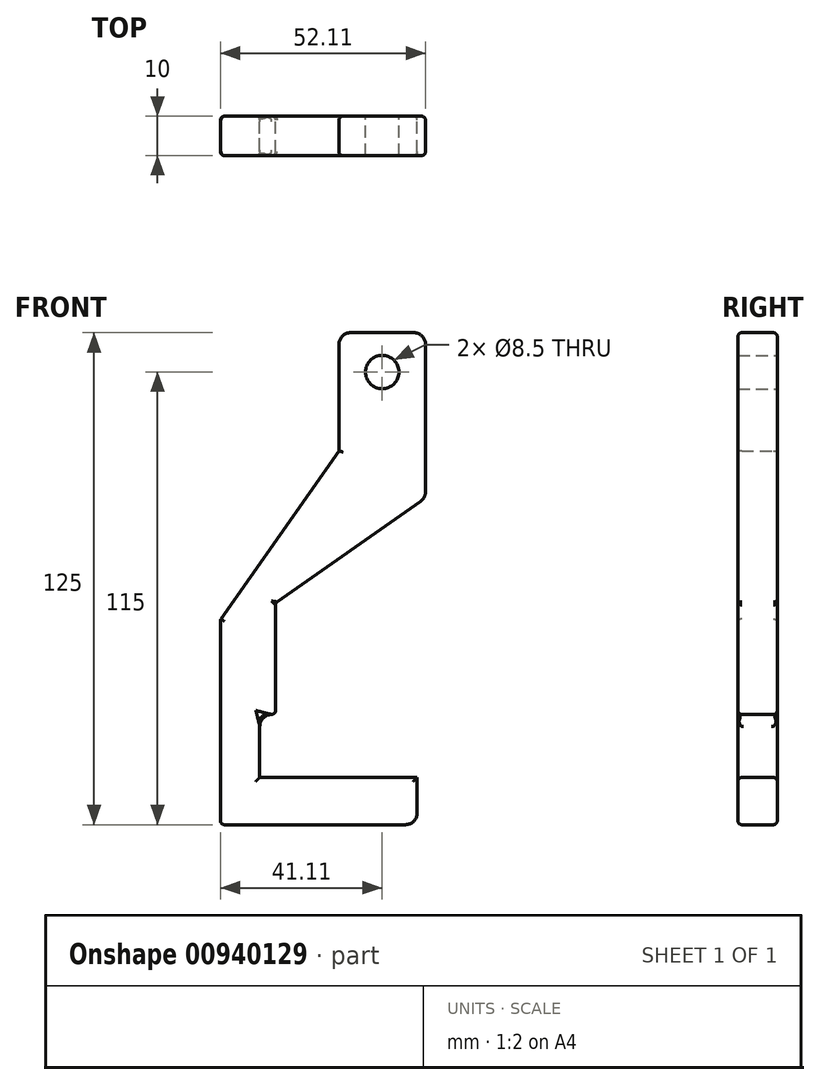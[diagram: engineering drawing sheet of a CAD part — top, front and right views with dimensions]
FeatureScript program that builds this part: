
annotation { "Feature Type Name" : "Feature", "Feature Type Description" : "" }
export const myFeature = defineFeature(function(context is Context, id is Id, definition is map)
    precondition{}
    {
        {
            var Q0;
            Q0=qCreatedBy(makeId("Front.planeOp"),FACE);
            var sketch = newSketch(context, id + "F0", { "sketchPlane" : qUnion([Q0])});
            skCircle(sketch, "E0", {"center": v(0, 0) * mm, "radius": 4.25 * mm});
            skLineSegment(sketch, "E1", {"start": v(0, 0) * mm, "end": v(0, 4.25) * mm});
            skLineSegment(sketch, "E2", {"start": v(0, 10) * mm, "end": v(-11, 10) * mm});
            skLineSegment(sketch, "E3", {"start": v(0, 10) * mm, "end": v(11, 10) * mm});
            skLineSegment(sketch, "E4", {"start": v(11, 10) * mm, "end": v(11, -32) * mm});
            skLineSegment(sketch, "E5", {"start": v(-11, 10) * mm, "end": v(-11, -20) * mm});
            skLineSegment(sketch, "E6", {"start": v(-41.1, -115) * mm, "end": v(-41.1, -63) * mm});
            skLineSegment(sketch, "E7", {"start": v(-41.1, -115) * mm, "end": v(8.9, -115) * mm});
            skLineSegment(sketch, "E8", {"start": v(8.9, -115) * mm, "end": v(8.9, -103) * mm});
            skLineSegment(sketch, "E9", {"start": v(8.9, -103) * mm, "end": v(-31.1, -103) * mm});
            skLineSegment(sketch, "E10", {"start": v(-31.1, -103) * mm, "end": v(-31.1, -87) * mm});
            skLineSegment(sketch, "E11", {"start": v(-31.1, -87) * mm, "end": v(-27.1, -87) * mm});
            skLineSegment(sketch, "E12", {"start": v(-27.1, -87) * mm, "end": v(-27.1, -58.68) * mm});
            skLineSegment(sketch, "E13", {"start": v(-41.1, -63) * mm, "end": v(-11, -20) * mm});
            skLineSegment(sketch, "E14", {"start": v(11, -32) * mm, "end": v(-27.1, -58.68) * mm});
            skSolve(sketch);
        }
        {
            var Q0;
            Q0=makeQuery(id+"F0.imprint","IMPRINT",FACE,{"disambiguationData":[TD([[makeQuery(id+"F0.imprint","IMPRINT",EDGE,{"derivedFrom":sQuery(id+"F0.wireOp",EDGE,"E0")}),-1.0]])]});
            extrude(context, id + "F1", {"entities" : qUnion([Q0]), "depth" : 10 * mm, "offsetDistance" : 25 * mm});
        }
        {
            var Q0;
            Q0=makeQuery(id+"F1.opExtrude","CAP_EDGE",EDGE,{"disambiguationData":[OSD([sQuery(id+"F0.wireOp",EDGE,"E5")])],"isStart":false});
            var Q1;
            Q1=makeQuery(id+"F1.opExtrude","CAP_EDGE",EDGE,{"disambiguationData":[OSD([sQuery(id+"F0.wireOp",EDGE,"E13")])],"isStart":false});
            var Q2;
            Q2=makeQuery(id+"F1.opExtrude","CAP_EDGE",EDGE,{"disambiguationData":[OSD([sQuery(id+"F0.wireOp",EDGE,"E6")])],"isStart":true});
            var Q3;
            Q3=makeQuery(id+"F1.opExtrude","CAP_EDGE",EDGE,{"disambiguationData":[OSD([sQuery(id+"F0.wireOp",EDGE,"E2"),sQuery(id+"F0.wireOp",EDGE,"E3")])],"isStart":false});
            var Q4;
            Q4=makeQuery(id+"F1.opExtrude","CAP_EDGE",EDGE,{"disambiguationData":[OSD([sQuery(id+"F0.wireOp",EDGE,"E4")])],"isStart":false});
            var Q5;
            Q5=makeQuery(id+"F1.opExtrude","CAP_EDGE",EDGE,{"disambiguationData":[OSD([sQuery(id+"F0.wireOp",EDGE,"E14")])],"isStart":false});
            var Q6;
            Q6=makeQuery(id+"F1.opExtrude","CAP_EDGE",EDGE,{"disambiguationData":[OSD([sQuery(id+"F0.wireOp",EDGE,"E12")])],"isStart":false});
            var Q7;
            Q7=makeQuery(id+"F1.opExtrude","CAP_EDGE",EDGE,{"disambiguationData":[OSD([sQuery(id+"F0.wireOp",EDGE,"E7")])],"isStart":false});
            var Q8;
            Q8=makeQuery(id+"F1.opExtrude","CAP_EDGE",EDGE,{"disambiguationData":[OSD([sQuery(id+"F0.wireOp",EDGE,"E8")])],"isStart":false});
            var Q9;
            Q9=makeQuery(id+"F1.opExtrude","CAP_EDGE",EDGE,{"disambiguationData":[OSD([sQuery(id+"F0.wireOp",EDGE,"E9")])],"isStart":false});
            var Q10;
            Q10=makeQuery(id+"F1.opExtrude","CAP_EDGE",EDGE,{"disambiguationData":[OSD([sQuery(id+"F0.wireOp",EDGE,"E10")])],"isStart":false});
            var Q11;
            Q11=makeQuery(id+"F1.opExtrude","CAP_EDGE",EDGE,{"disambiguationData":[OSD([sQuery(id+"F0.wireOp",EDGE,"E11")])],"isStart":false});
            var Q12;
            Q12=makeQuery(id+"F1.opExtrude","CAP_EDGE",EDGE,{"disambiguationData":[OSD([sQuery(id+"F0.wireOp",EDGE,"E8")])],"isStart":true});
            var Q13;
            Q13=makeQuery(id+"F1.opExtrude","CAP_EDGE",EDGE,{"disambiguationData":[OSD([sQuery(id+"F0.wireOp",EDGE,"E9")])],"isStart":true});
            var Q14;
            Q14=makeQuery(id+"F1.opExtrude","CAP_EDGE",EDGE,{"disambiguationData":[OSD([sQuery(id+"F0.wireOp",EDGE,"E10")])],"isStart":true});
            var Q15;
            Q15=makeQuery(id+"F1.opExtrude","CAP_EDGE",EDGE,{"disambiguationData":[OSD([sQuery(id+"F0.wireOp",EDGE,"E11")])],"isStart":true});
            var Q16;
            Q16=makeQuery(id+"F1.opExtrude","CAP_EDGE",EDGE,{"disambiguationData":[OSD([sQuery(id+"F0.wireOp",EDGE,"E14")])],"isStart":true});
            var Q17;
            Q17=makeQuery(id+"F1.opExtrude","CAP_EDGE",EDGE,{"disambiguationData":[OSD([sQuery(id+"F0.wireOp",EDGE,"E4")])],"isStart":true});
            var Q18;
            Q18=makeQuery(id+"F1.opExtrude","CAP_EDGE",EDGE,{"disambiguationData":[OSD([sQuery(id+"F0.wireOp",EDGE,"E13")])],"isStart":true});
            var Q19;
            Q19=makeQuery(id+"F1.opExtrude","SWEPT_EDGE",EDGE,{"disambiguationData":[OSD([sQuery(id+"F0.wireOp",EDGE,"E6"),sQuery(id+"F0.wireOp",EDGE,"E7")])]});
            var Q20;
            Q20=makeQuery(id+"F1.opExtrude","CAP_EDGE",EDGE,{"disambiguationData":[OSD([sQuery(id+"F0.wireOp",EDGE,"E7")])],"isStart":true});
            var Q21;
            Q21=makeQuery(id+"F1.opExtrude","CAP_EDGE",EDGE,{"disambiguationData":[OSD([sQuery(id+"F0.wireOp",EDGE,"E2"),sQuery(id+"F0.wireOp",EDGE,"E3")])],"isStart":true});
            var Q22;
            Q22=makeQuery(id+"F1.opExtrude","CAP_EDGE",EDGE,{"disambiguationData":[OSD([sQuery(id+"F0.wireOp",EDGE,"E5")])],"isStart":true});
            fillet(context, id + "F2", {"entities" : qUnion([Q0, Q1, Q2, Q3, Q4, Q5, Q6, Q7, Q8, Q9, Q10, Q11, Q12, Q13, Q14, Q15, Q16, Q17, Q18, Q19, Q20, Q21, Q22]), "radius" : 1 * mm, "tangentPropagation" : true, "allowEdgeOverflow" : false});
        }
        {
            var Q0;
            Q0=makeQuery(id+"F1.opExtrude","SWEPT_EDGE",EDGE,{"disambiguationData":[OSD([sQuery(id+"F0.wireOp",EDGE,"E2"),sQuery(id+"F0.wireOp",EDGE,"E5")])]});
            var Q1;
            Q1=makeQuery(id+"F1.opExtrude","SWEPT_EDGE",EDGE,{"disambiguationData":[OSD([sQuery(id+"F0.wireOp",EDGE,"E3"),sQuery(id+"F0.wireOp",EDGE,"E4")])]});
            var Q2;
            Q2=makeQuery(id+"F1.opExtrude","SWEPT_EDGE",EDGE,{"disambiguationData":[OSD([sQuery(id+"F0.wireOp",EDGE,"E7"),sQuery(id+"F0.wireOp",EDGE,"E8")])]});
            var Q3;
            Q3=makeQuery(id+"F1.opExtrude","SWEPT_EDGE",EDGE,{"disambiguationData":[OSD([sQuery(id+"F0.wireOp",EDGE,"E4"),sQuery(id+"F0.wireOp",EDGE,"E14")])]});
            var Q4;
            Q4=makeQuery(id+"F1.opExtrude","SWEPT_EDGE",EDGE,{"disambiguationData":[OSD([sQuery(id+"F0.wireOp",EDGE,"E10"),sQuery(id+"F0.wireOp",EDGE,"E11")])]});
            fillet(context, id + "F3", {"entities" : qUnion([Q0, Q1, Q2, Q3, Q4]), "radius" : 3 * mm, "tangentPropagation" : true, "allowEdgeOverflow" : false});
        }
        {
            var Q0;
            Q0=makeQuery(id+"F1.opExtrude","SWEPT_EDGE",EDGE,{"disambiguationData":[OSD([sQuery(id+"F0.wireOp",EDGE,"E11"),sQuery(id+"F0.wireOp",EDGE,"E12")])]});
            fillet(context, id + "F4", {"entities" : qUnion([Q0]), "radius" : 1 * mm, "tangentPropagation" : true, "allowEdgeOverflow" : false});
        }
        {
            var Q0;
            Q0=makeQuery(id+"F1.opExtrude","CAP_EDGE",EDGE,{"disambiguationData":[OSD([sQuery(id+"F0.wireOp",EDGE,"E6")])],"isStart":false});
            var Q1;
            Q1=makeQuery(id+"F1.opExtrude","SWEPT_EDGE",EDGE,{"disambiguationData":[OSD([sQuery(id+"F0.wireOp",EDGE,"E12"),sQuery(id+"F0.wireOp",EDGE,"E14")])]});
            fillet(context, id + "F5", {"entities" : qUnion([Q0, Q1]), "radius" : 1 * mm, "tangentPropagation" : true, "allowEdgeOverflow" : false});
        }
    });
